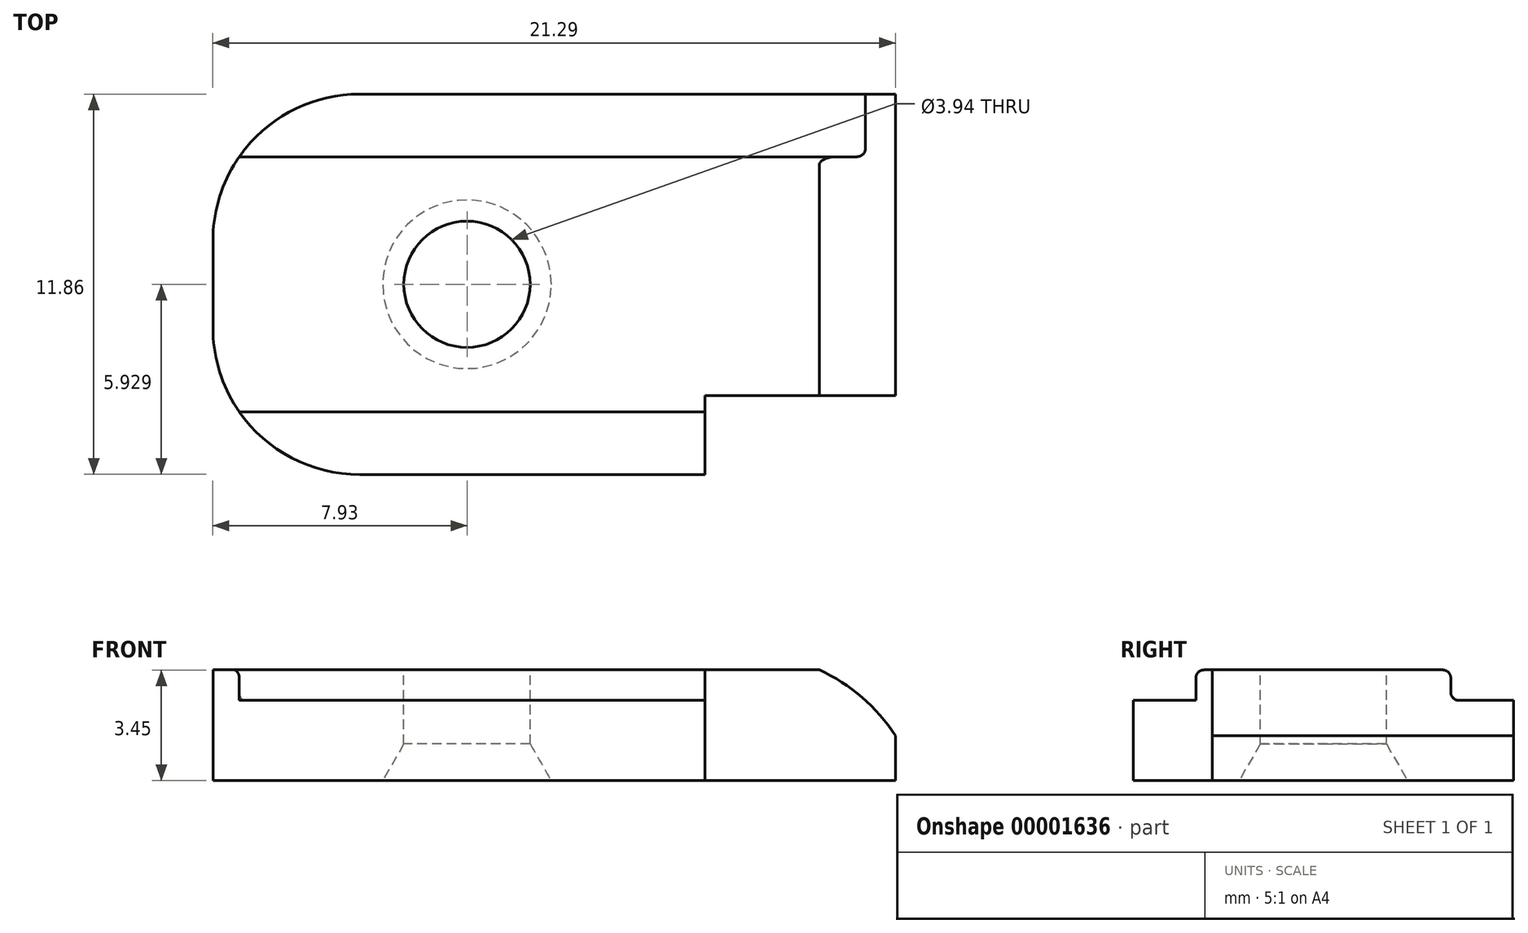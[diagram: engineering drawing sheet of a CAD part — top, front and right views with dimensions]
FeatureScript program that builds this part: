
annotation { "Feature Type Name" : "Feature", "Feature Type Description" : "" }
export const myFeature = defineFeature(function(context is Context, id is Id, definition is map)
    precondition{}
    {
        {
            var Q0;
            Q0=qCreatedBy(makeId("Top.planeOp"),FACE);
            var sketch = newSketch(context, id + "F0", { "sketchPlane" : qUnion([Q0])});
            skLineSegment(sketch, "E0", {"start": v(0, 0) * mm, "end": v(-16.71, 0) * mm});
            skLineSegment(sketch, "E1", {"start": v(0, 0) * mm, "end": v(0, -9.4) * mm});
            skLineSegment(sketch, "E2", {"start": v(0, -9.4) * mm, "end": v(-5.94, -9.4) * mm});
            skLineSegment(sketch, "E3", {"start": v(-5.94, -9.4) * mm, "end": v(-5.94, -11.86) * mm});
            skLineSegment(sketch, "E4", {"start": v(-5.94, -11.86) * mm, "end": v(-16.71, -11.86) * mm});
            skLineSegment(sketch, "E5", {"start": v(-21.29, -7.29) * mm, "end": v(-21.29, -4.57) * mm});
            skArc(sketch, "E6", {"start": v(-16.71, 0) * mm, "mid": v(-19.95, -1.34) * mm, "end": v(-21.29, -4.57) * mm});
            skArc(sketch, "E7", {"start": v(-16.71, -11.86) * mm, "mid": v(-19.95, -10.52) * mm, "end": v(-21.29, -7.29) * mm});
            skSolve(sketch);
        }
        {
            var Q0;
            Q0=makeQuery(id+"F0.imprint","IMPRINT",FACE,{"disambiguationData":[TD([[makeQuery(id+"F0.imprint","IMPRINT",EDGE,{"derivedFrom":sQuery(id+"F0.wireOp",EDGE,"E0")}),1.0]])]});
            extrude(context, id + "F1", {"entities" : qUnion([Q0]), "depth" : 2.5 * mm});
        }
        {
            var Q0;
            Q0=makeQuery(id+"F1.opExtrude","CAP_FACE",FACE,{"disambiguationData":[OSD([sQuery(id+"F0.wireOp",EDGE,"E0"),sQuery(id+"F0.wireOp",EDGE,"E1"),sQuery(id+"F0.wireOp",EDGE,"E2"),sQuery(id+"F0.wireOp",EDGE,"E3"),sQuery(id+"F0.wireOp",EDGE,"E4"),sQuery(id+"F0.wireOp",EDGE,"E5"),sQuery(id+"F0.wireOp",EDGE,"E6"),sQuery(id+"F0.wireOp",EDGE,"E7")])],"isStart":false});
            var sketch = newSketch(context, id + "F2", { "sketchPlane" : qUnion([Q0])});
            skLineSegment(sketch, "E8", {"start": v(-21.29, -5.93) * mm, "end": v(0, -5.93) * mm, "construction": true});
            skLineSegment(sketch, "E9", {"start": v(-20.46, -1.96) * mm, "end": v(0, -1.96) * mm});
            skLineSegment(sketch, "E10", {"start": v(-5.94, -9.9) * mm, "end": v(-20.46, -9.9) * mm});
            skLineSegment(sketch, "E11", {"start": v(-15.79, -9.9) * mm, "end": v(-15.79, -5.93) * mm, "construction": true});
            skLineSegment(sketch, "E12", {"start": v(-15.79, -5.93) * mm, "end": v(-15.79, -1.96) * mm, "construction": true});
            skSolve(sketch);
        }
        {
            var Q0;
            {var subQ4=sQuery(id+"F2.wireOp",EDGE,"E9");Q0=makeQuery(id+"F2.imprint","IMPRINT",FACE,{"disambiguationData":[TD([[makeQuery(id+"F2.imprint","IMPRINT",EDGE,{"derivedFrom":subQ4}),-1.0]])]});}
            extrude(context, id + "F3", {"entities" : qUnion([Q0]), "operationType" : NewBodyOperationType.ADD, "depth" : 0.95 * mm});
        }
        {
            var Q0;
            Q0=makeQuery(id+"F3.opExtrude","CAP_FACE",FACE,{"disambiguationData":[OSD([sQuery(id+"F0.wireOp",EDGE,"E1"),sQuery(id+"F0.wireOp",EDGE,"E2"),sQuery(id+"F0.wireOp",EDGE,"E3"),sQuery(id+"F0.wireOp",EDGE,"E5"),sQuery(id+"F0.wireOp",EDGE,"E6"),sQuery(id+"F0.wireOp",EDGE,"E7"),sQuery(id+"F2.wireOp",EDGE,"E9"),sQuery(id+"F2.wireOp",EDGE,"E10")])],"isStart":false});
            var sketch = newSketch(context, id + "F4", { "sketchPlane" : qUnion([Q0])});
            skCircle(sketch, "E13", {"center": v(-13.36, -5.93) * mm, "radius": 1.97 * mm});
            skPoint(sketch, "E14", {"position": v(-21.29, -5.93) * mm});
            skSolve(sketch);
        }
        {
            var Q0;
            Q0=makeQuery(id+"F4.imprint","IMPRINT",FACE,{"disambiguationData":[TD([[makeQuery(id+"F4.imprint","IMPRINT",EDGE,{"derivedFrom":sQuery(id+"F4.wireOp",EDGE,"E13")}),1.0]])]});
            extrude(context, id + "F5", {"entities" : qUnion([Q0]), "operationType" : NewBodyOperationType.REMOVE, "endBound" : BoundingType.THROUGH_ALL, "oppositeDirection" : true, "depth" : 25.4 * mm});
        }
        {
            var Q0;
            Q0=makeQuery(id+"F5.boolean.opBoolean","INTERSECT",EDGE,{"derivedFrom":[makeQuery(id+"F1.opExtrude","CAP_FACE",FACE,{"disambiguationData":[OSD([sQuery(id+"F0.wireOp",EDGE,"E0"),sQuery(id+"F0.wireOp",EDGE,"E1"),sQuery(id+"F0.wireOp",EDGE,"E2"),sQuery(id+"F0.wireOp",EDGE,"E3"),sQuery(id+"F0.wireOp",EDGE,"E4"),sQuery(id+"F0.wireOp",EDGE,"E5"),sQuery(id+"F0.wireOp",EDGE,"E6"),sQuery(id+"F0.wireOp",EDGE,"E7")])],"isStart":true}),makeQuery(id+"F5.opExtrude","SWEPT_FACE",FACE,{"disambiguationData":[OSD([sQuery(id+"F4.wireOp",EDGE,"E13")])]})]});
            chamfer(context, id + "F6", {"entities" : qUnion([Q0]), "chamferType" : ChamferType.OFFSET_ANGLE, "width" : 0.66 * mm, "oppositeDirection" : false, "angle" : 60 * degree, "tangentPropagation" : true});
        }
        {
            var Q0;
            {var subQ0=sQuery(id+"F0.wireOp",EDGE,"E2");Q0=makeQuery(id+"F3.boolean.opBoolean","MERGE",FACE,{"derivedFrom":[makeQuery(id+"F1.opExtrude","SWEPT_FACE",FACE,{"disambiguationData":[OSD([subQ0])]}),makeQuery(id+"F3.opExtrude","SWEPT_FACE",FACE,{"disambiguationData":[OSD([subQ0])]})]});}
            var sketch = newSketch(context, id + "F7", { "sketchPlane" : qUnion([Q0])});
            skCircle(sketch, "E15", {"center": v(-4.7, -1.63) * mm, "radius": 5.59 * mm});
            skSolve(sketch);
        }
        {
            var Q0;
            {var subQ1=sQuery(id+"F0.wireOp",EDGE,"E2");var subQ3=sQuery(id+"F7.wireOp",EDGE,"E15");var subQ5=makeQuery(id+"F3.opExtrude","CAP_EDGE",EDGE,{"disambiguationData":[OSD([subQ1])],"isStart":false});var subQ7=makeQuery(id+"F7.imprint","INTERSECT",VERTEX,{"derivedFrom":[subQ5,subQ3]});Q0=makeQuery(id+"F7.imprint","IMPRINT",FACE,{"disambiguationData":[TD([[makeQuery(id+"F7.imprint","IMPRINT",EDGE,{"disambiguationData":[TD([[subQ7,1.0]])],"derivedFrom":subQ3}),-1.0]])]});}
            extrude(context, id + "F8", {"entities" : qUnion([Q0]), "operationType" : NewBodyOperationType.REMOVE, "oppositeDirection" : true, "depth" : 25.4 * mm});
        }
        {
            var Q0;
            Q0=makeQuery(id+"F3.opExtrude","CAP_EDGE",EDGE,{"disambiguationData":[OSD([sQuery(id+"F2.wireOp",EDGE,"E10")])],"isStart":true});
            var Q1;
            Q1=makeQuery(id+"F3.opExtrude","CAP_EDGE",EDGE,{"disambiguationData":[OSD([sQuery(id+"F2.wireOp",EDGE,"E10")])],"isStart":false});
            var Q2;
            Q2=makeQuery(id+"F3.opExtrude","CAP_EDGE",EDGE,{"disambiguationData":[OSD([sQuery(id+"F2.wireOp",EDGE,"E9")])],"isStart":true});
            var Q3;
            Q3=makeQuery(id+"F3.opExtrude","CAP_EDGE",EDGE,{"disambiguationData":[OSD([sQuery(id+"F2.wireOp",EDGE,"E9")])],"isStart":false});
            fillet(context, id + "F9", {"entities" : qUnion([Q0, Q1, Q2, Q3]), "radius" : 0.25 * mm, "tangentPropagation" : true, "allowEdgeOverflow" : false});
        }
    });
